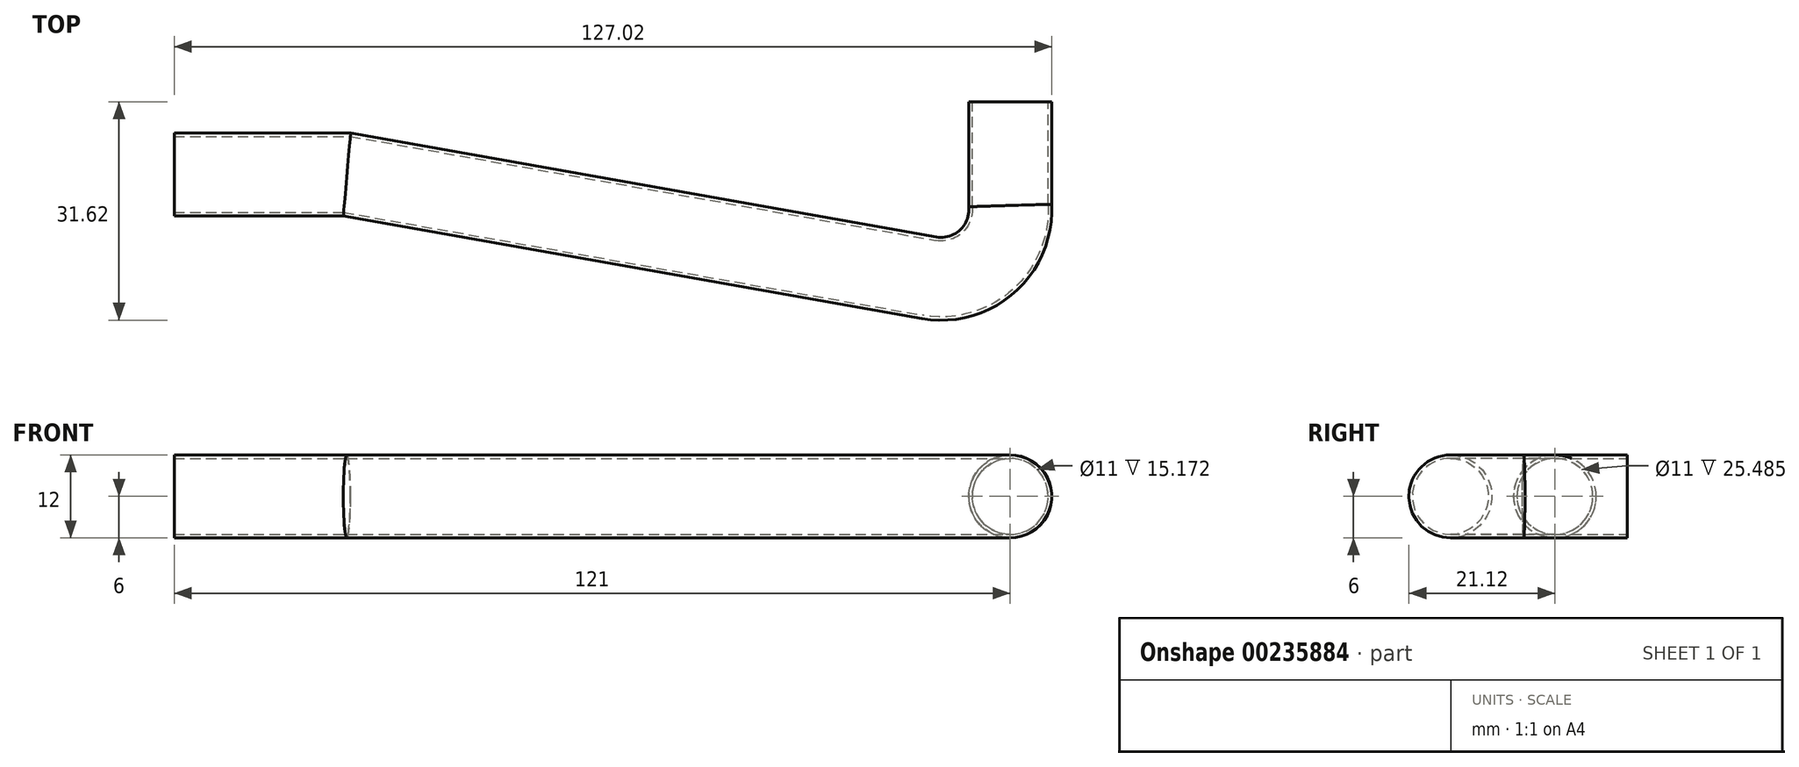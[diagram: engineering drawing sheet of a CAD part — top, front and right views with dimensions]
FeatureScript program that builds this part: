
annotation { "Feature Type Name" : "Feature", "Feature Type Description" : "" }
export const myFeature = defineFeature(function(context is Context, id is Id, definition is map)
    precondition{}
    {
        {
            var Q0;
            Q0=qCreatedBy(makeId("Top.planeOp"),FACE);
            var sketch = newSketch(context, id + "F0", { "sketchPlane" : qUnion([Q0])});
            skLineSegment(sketch, "E0", {"start": v(0, 0) * mm, "end": v(25, 0) * mm});
            skLineSegment(sketch, "E1", {"start": v(0, 0) * mm, "end": v(0, -12) * mm});
            skLineSegment(sketch, "E2", {"start": v(0, -12) * mm, "end": v(25, -12) * mm});
            skLineSegment(sketch, "E3", {"start": v(25, -12) * mm, "end": v(25, 0) * mm});
            skLineSegment(sketch, "E4", {"start": v(0, 0) * mm, "end": v(0, -6) * mm});
            skLineSegment(sketch, "E5", {"start": v(0, -6) * mm, "end": v(0, 4.5) * mm});
            skLineSegment(sketch, "E6", {"start": v(0, 4.5) * mm, "end": v(121, 4.5) * mm, "construction": true});
            skLineSegment(sketch, "E7", {"start": v(121, 4.5) * mm, "end": v(127, 4.5) * mm});
            skLineSegment(sketch, "E8", {"start": v(127, 4.5) * mm, "end": v(115, 4.5) * mm});
            skLineSegment(sketch, "E9", {"start": v(127, 4.5) * mm, "end": v(127, -10.5) * mm});
            skLineSegment(sketch, "E10", {"start": v(127, -10.5) * mm, "end": v(115, -10.5) * mm});
            skLineSegment(sketch, "E11", {"start": v(115, -10.5) * mm, "end": v(115, 4.5) * mm});
            skLineSegment(sketch, "E12", {"start": v(0, -6) * mm, "end": v(25, -6) * mm});
            skLineSegment(sketch, "E13", {"start": v(121, 4.5) * mm, "end": v(121, -10.5) * mm});
            skPoint(sketch, "E13.endSnap0", {"position": v(121, -10.5) * mm});
            skArc(sketch, "E14", {"start": v(109.27, -20.97) * mm, "mid": v(117.68, -18.58) * mm, "end": v(121, -10.5) * mm});
            skPoint(sketch, "E14.second.point", {"position": v(121, -14.76) * mm});
            skLineSegment(sketch, "E15", {"start": v(25, -6) * mm, "end": v(109.27, -20.97) * mm});
            skLineSegment(sketch, "E16", {"start": v(109.27, -20.97) * mm, "end": v(146.51, -27.59) * mm});
            skLineSegment(sketch, "E17", {"start": v(121, -10.5) * mm, "end": v(121, -27.72) * mm});
            skLineSegment(sketch, "E18", {"start": v(121, 4.5) * mm, "end": v(121, 17.85) * mm});
            skLineSegment(sketch, "E19", {"start": v(121, 4.5) * mm, "end": v(113.88, 4.5) * mm});
            skLineSegment(sketch, "E20", {"start": v(113.88, 4.5) * mm, "end": v(113.88, 26.56) * mm});
            skLineSegment(sketch, "E21", {"start": v(127, 4.5) * mm, "end": v(129.1, 4.5) * mm});
            skLineSegment(sketch, "E22", {"start": v(129.1, 4.5) * mm, "end": v(129.1, 26.56) * mm});
            skLineSegment(sketch, "E23", {"start": v(129.1, 26.56) * mm, "end": v(113.88, 26.56) * mm});
            skSolve(sketch);
        }
        {
            var Q0;
            Q0=qCreatedBy(makeId("Right.planeOp"),FACE);
            var sketch = newSketch(context, id + "F1", { "sketchPlane" : qUnion([Q0])});
            skCircle(sketch, "E24", {"center": v(-6, 0) * mm, "radius": 6 * mm});
            skCircle(sketch, "E25.0", {"center": v(-6, 0) * mm, "radius": 5.5 * mm});
            skLineSegment(sketch, "E26", {"start": v(0, 0) * mm, "end": v(0, 3.6) * mm});
            skSolve(sketch);
        }
        {
            var Q0;
            Q0=makeQuery(id+"F1.imprint","IMPRINT",FACE,{"disambiguationData":[TD([[makeQuery(id+"F1.imprint","IMPRINT",EDGE,{"derivedFrom":sQuery(id+"F1.wireOp",EDGE,"E24")}),1.0]])]});
            var Q1;
            Q1=sQuery(id+"F0.wireOp",EDGE,"E12");
            var Q2;
            Q2=sQuery(id+"F0.wireOp",EDGE,"E15");
            var Q3;
            Q3=sQuery(id+"F0.wireOp",EDGE,"E14");
            var Q4;
            Q4=sQuery(id+"F0.wireOp",EDGE,"E13");
            var Q5;
            Q5=sQuery(id+"F0.wireOp",EDGE,"E18");
            sweep(context, id + "F2", {"profiles" : qUnion([Q0]), "path" : qUnion([Q1, Q2, Q3, Q4, Q5])});
        }
        {
            var Q0;
            {var subQ3=sQuery(id+"F0.wireOp",EDGE,"E8");Q0=makeQuery(id+"F0.imprint","IMPRINT",FACE,{"disambiguationData":[TD([[makeQuery(id+"F0.imprint","IMPRINT",EDGE,{"derivedFrom":subQ3}),-1.0]])]});}
            extrude(context, id + "F3", {"entities" : qUnion([Q0]), "operationType" : NewBodyOperationType.REMOVE, "oppositeDirection" : true, "depth" : 25 * mm, "symmetric" : true});
        }
    });
